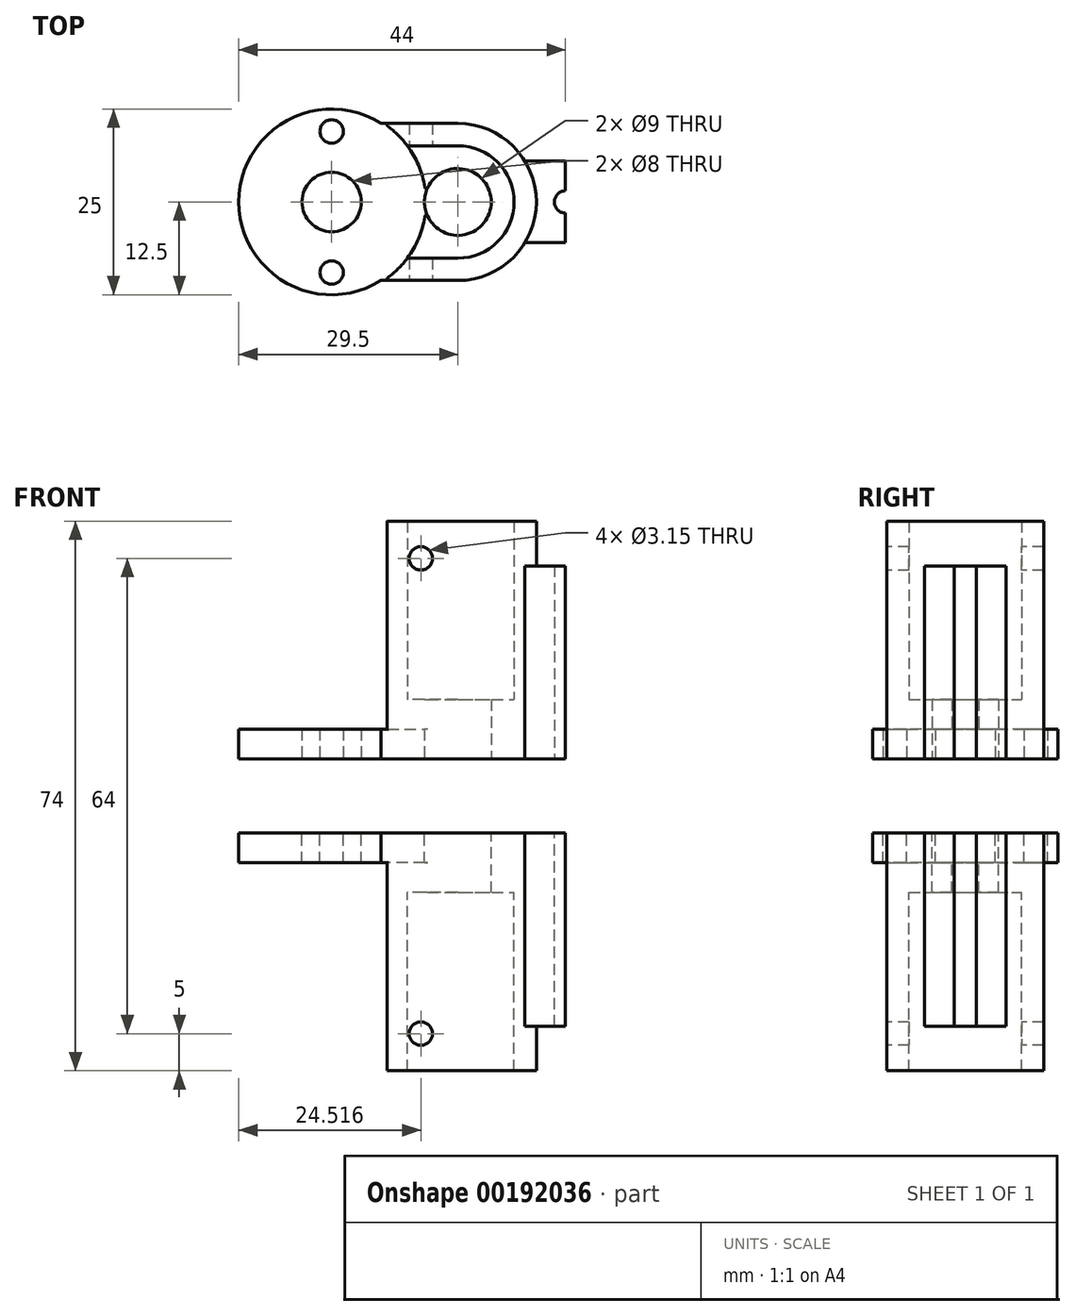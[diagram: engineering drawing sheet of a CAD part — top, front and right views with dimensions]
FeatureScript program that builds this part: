
annotation { "Feature Type Name" : "Feature", "Feature Type Description" : "" }
export const myFeature = defineFeature(function(context is Context, id is Id, definition is map)
    precondition{}
    {
        {
            var Q0;
            Q0=qCreatedBy(makeId("Top.planeOp"),FACE);
            var sketch = newSketch(context, id + "F0", { "sketchPlane" : qUnion([Q0])});
            skCircle(sketch, "E0", {"center": v(0, 0) * mm, "radius": 4 * mm, "construction": true});
            skCircle(sketch, "E1", {"center": v(17, 0) * mm, "radius": 4.5 * mm, "construction": true});
            skCircle(sketch, "E2", {"center": v(17, 0) * mm, "radius": 7.58 * mm, "construction": true});
            skCircle(sketch, "E3", {"center": v(31.5, 0) * mm, "radius": 9 * mm, "construction": true});
            skArc(sketch, "E4", {"start": v(31.5, 7.5) * mm, "mid": v(39, 0) * mm, "end": v(31.5, -7.5) * mm, "construction": true});
            skLineSegment(sketch, "E5", {"start": v(31.5, 7.5) * mm, "end": v(-52.72, 7.5) * mm, "construction": true});
            skLineSegment(sketch, "E6", {"start": v(31.5, -7.5) * mm, "end": v(-52.72, -7.5) * mm, "construction": true});
            skCircle(sketch, "E7", {"center": v(31.5, 0) * mm, "radius": 1.5 * mm, "construction": true});
            skArc(sketch, "E8", {"start": v(31.5, 5.5) * mm, "mid": v(37, 0) * mm, "end": v(31.5, -5.5) * mm, "construction": true});
            skLineSegment(sketch, "E9", {"start": v(31.5, 5.5) * mm, "end": v(-52.72, 5.5) * mm, "construction": true});
            skLineSegment(sketch, "E10", {"start": v(31.5, -5.5) * mm, "end": v(-52.72, -5.5) * mm, "construction": true});
            skCircle(sketch, "E11", {"center": v(0, 0) * mm, "radius": 12.5 * mm, "construction": true});
            skLineSegment(sketch, "E12", {"start": v(-52.72, 7.5) * mm, "end": v(-52.72, 5.5) * mm, "construction": true});
            skLineSegment(sketch, "E13", {"start": v(-52.72, -5.5) * mm, "end": v(-52.72, -7.5) * mm, "construction": true});
            skLineSegment(sketch, "E14", {"start": v(22.5, 0) * mm, "end": v(21.5, 0) * mm, "construction": true});
            skCircle(sketch, "E15", {"center": v(0, 9.5) * mm, "radius": 1.57 * mm, "construction": true});
            skCircle(sketch, "E16.MirrorC", {"center": v(0, -9.5) * mm, "radius": 1.57 * mm, "construction": true});
            skSolve(sketch);
        }
        {
            var Q0;
            Q0=qCreatedBy(makeId("Front.planeOp"),FACE);
            var sketch = newSketch(context, id + "F1", { "sketchPlane" : qUnion([Q0])});
            skLineSegment(sketch, "E17.bottom", {"start": v(-49.85, 26.5) * mm, "end": v(65.27, 26.5) * mm});
            skLineSegment(sketch, "E17.top", {"start": v(-49.85, 18.5) * mm, "end": v(65.27, 18.5) * mm});
            skLineSegment(sketch, "E17.left", {"start": v(-49.85, 26.5) * mm, "end": v(-49.85, 18.5) * mm});
            skLineSegment(sketch, "E17.right", {"start": v(65.27, 26.5) * mm, "end": v(65.27, 18.5) * mm});
            skLineSegment(sketch, "E18.MirrorCS", {"start": v(-49.85, -26.5) * mm, "end": v(-49.85, -18.5) * mm});
            skLineSegment(sketch, "E19.MirrorCS", {"start": v(-49.85, -26.5) * mm, "end": v(65.27, -26.5) * mm});
            skLineSegment(sketch, "E20.MirrorCS", {"start": v(-49.85, -18.5) * mm, "end": v(65.27, -18.5) * mm});
            skLineSegment(sketch, "E21.MirrorCS", {"start": v(65.27, -26.5) * mm, "end": v(65.27, -18.5) * mm});
            skPoint(sketch, "E22", {"position": v(-49.85, 22.5) * mm});
            skPoint(sketch, "E23", {"position": v(-49.85, -22.5) * mm});
            skSolve(sketch);
        }
        {
            var Q0;
            Q0=qCreatedBy(makeId("Top.planeOp"),FACE);
            var sketch = newSketch(context, id + "F2", { "sketchPlane" : qUnion([Q0])});
            skCircle(sketch, "E24.0", {"center": v(0, 0) * mm, "radius": 12.5 * mm, "construction": true});
            skCircle(sketch, "E25.0", {"center": v(17, 0) * mm, "radius": 7.58 * mm, "construction": true});
            skCircle(sketch, "E26.0", {"center": v(31.5, 0) * mm, "radius": 9 * mm, "construction": true});
            skCircle(sketch, "E27.0", {"center": v(17, 0) * mm, "radius": 10.58 * mm, "construction": true});
            skLineSegment(sketch, "E28", {"start": v(17, 10.58) * mm, "end": v(6.66, 10.57) * mm});
            skLineSegment(sketch, "E29", {"start": v(17, -10.58) * mm, "end": v(6.66, -10.58) * mm});
            skArc(sketch, "E30", {"start": v(6.66, 10.57) * mm, "mid": v(-12.5, 0) * mm, "end": v(6.66, -10.58) * mm});
            skArc(sketch, "E31.0", {"start": v(31.5, 5.5) * mm, "mid": v(37, 0) * mm, "end": v(31.5, -5.5) * mm, "construction": true});
            skLineSegment(sketch, "E32", {"start": v(31.5, 5.5) * mm, "end": v(26.03, 5.5) * mm});
            skLineSegment(sketch, "E33", {"start": v(31.5, -5.5) * mm, "end": v(26.03, -5.5) * mm});
            skArc(sketch, "E34", {"start": v(17, 10.58) * mm, "mid": v(22.18, 9.22) * mm, "end": v(26.03, 5.5) * mm});
            skArc(sketch, "E35", {"start": v(17, -10.58) * mm, "mid": v(22.18, -9.22) * mm, "end": v(26.03, -5.5) * mm});
            skCircle(sketch, "E36.0", {"center": v(0, 0) * mm, "radius": 4 * mm});
            skCircle(sketch, "E37.0", {"center": v(31.5, 0) * mm, "radius": 1.5 * mm});
            skCircle(sketch, "E38.0", {"center": v(17, 0) * mm, "radius": 4.5 * mm});
            skLineSegment(sketch, "E39", {"start": v(31.5, 5.5) * mm, "end": v(31.5, 1.5) * mm});
            skLineSegment(sketch, "E40", {"start": v(31.5, -5.5) * mm, "end": v(31.5, -1.5) * mm});
            skCircle(sketch, "E41.0", {"center": v(0, 9.5) * mm, "radius": 1.57 * mm});
            skCircle(sketch, "E42.0", {"center": v(0, -9.5) * mm, "radius": 1.57 * mm});
            skSolve(sketch);
        }
        {
            var Q0;
            Q0=qCreatedBy(makeId("Top.planeOp"),FACE);
            var sketch = newSketch(context, id + "F3", { "sketchPlane" : qUnion([Q0])});
            skLineSegment(sketch, "E43.0", {"start": v(31.5, 5.5) * mm, "end": v(-52.72, 5.5) * mm});
            skLineSegment(sketch, "E44.0", {"start": v(31.5, 7.5) * mm, "end": v(-52.72, 7.5) * mm});
            skLineSegment(sketch, "E45.0", {"start": v(-52.72, -5.5) * mm, "end": v(-52.72, -7.5) * mm});
            skLineSegment(sketch, "E46.0", {"start": v(31.5, -5.5) * mm, "end": v(-52.72, -5.5) * mm});
            skLineSegment(sketch, "E47.0", {"start": v(31.5, -7.5) * mm, "end": v(-52.72, -7.5) * mm});
            skArc(sketch, "E48.0", {"start": v(31.5, 5.5) * mm, "mid": v(37, 0) * mm, "end": v(31.5, -5.5) * mm});
            skArc(sketch, "E49.0", {"start": v(31.5, 7.5) * mm, "mid": v(39, 0) * mm, "end": v(31.5, -7.5) * mm});
            skLineSegment(sketch, "E50.0", {"start": v(-52.72, 7.5) * mm, "end": v(-52.72, 5.5) * mm});
            skSolve(sketch);
        }
        {
            var Q0;
            Q0=makeQuery(id+"F2.imprint","IMPRINT",FACE,{"disambiguationData":[TD([[makeQuery(id+"F2.imprint","IMPRINT",EDGE,{"derivedFrom":sQuery(id+"F2.wireOp",EDGE,"E28")}),1.0]])]});
            extrude(context, id + "F4", {"entities" : qUnion([Q0]), "depth" : 4 * mm});
        }
        {
            var Q0;
            Q0=makeQuery(id+"F4.opExtrude","CAP_FACE",FACE,{"disambiguationData":[OSD([sQuery(id+"F2.wireOp",EDGE,"E28"),sQuery(id+"F2.wireOp",EDGE,"E29"),sQuery(id+"F2.wireOp",EDGE,"E30"),sQuery(id+"F2.wireOp",EDGE,"E31.0"),sQuery(id+"F2.wireOp",EDGE,"E32"),sQuery(id+"F2.wireOp",EDGE,"E33"),sQuery(id+"F2.wireOp",EDGE,"E34"),sQuery(id+"F2.wireOp",EDGE,"E35"),sQuery(id+"F2.wireOp",EDGE,"E36.0"),sQuery(id+"F2.wireOp",EDGE,"E37.0"),sQuery(id+"F2.wireOp",EDGE,"E38.0")])],"isStart":false});
            var sketch = newSketch(context, id + "F5", { "sketchPlane" : qUnion([Q0])});
            skCircle(sketch, "E51.0", {"center": v(17, 0) * mm, "radius": 4.5 * mm});
            skArc(sketch, "E52", {"start": v(17, 10.58) * mm, "mid": v(27.58, 0) * mm, "end": v(17, -10.58) * mm});
            skArc(sketch, "E53", {"start": v(6.66, 10.57) * mm, "mid": v(12.5, 0) * mm, "end": v(6.66, -10.58) * mm, "construction": true});
            skArc(sketch, "E54.0", {"start": v(7.03, 10.57) * mm, "mid": v(12.7, 0) * mm, "end": v(7.03, -10.58) * mm});
            skLineSegment(sketch, "E55", {"start": v(17, 10.57) * mm, "end": v(7.03, 10.57) * mm});
            skLineSegment(sketch, "E56", {"start": v(17, -10.58) * mm, "end": v(7.03, -10.58) * mm});
            skSolve(sketch);
        }
        {
            var Q0;
            {var subQ7=sQuery(id+"F5.wireOp",EDGE,"E55");Q0=makeQuery(id+"F5.imprint","IMPRINT",FACE,{"disambiguationData":[TD([[makeQuery(id+"F5.imprint","IMPRINT",EDGE,{"derivedFrom":subQ7}),1.0]])]});}
            extrude(context, id + "F6", {"entities" : qUnion([Q0]), "operationType" : NewBodyOperationType.ADD, "depth" : 4 * mm});
        }
        {
            var Q0;
            Q0=makeQuery(id+"F6.opExtrude","CAP_FACE",FACE,{"disambiguationData":[OSD([sQuery(id+"F5.wireOp",EDGE,"E51.0"),sQuery(id+"F5.wireOp",EDGE,"E52"),sQuery(id+"F5.wireOp",EDGE,"BbAhyjgk-xgWP-F3I1-mA0A-6WR5w57MHJqB"),sQuery(id+"F5.wireOp",EDGE,"622a587f-51d2-48ef-ab83-598356b288d1.0"),sQuery(id+"F5.wireOp",EDGE,"a473993c-0456-45ff-bfd1-ddf6d82de39f.0")])],"isStart":false});
            var sketch = newSketch(context, id + "F7", { "sketchPlane" : qUnion([Q0])});
            skCircle(sketch, "E57.0", {"center": v(17, 0) * mm, "radius": 7.58 * mm, "construction": true});
            skArc(sketch, "E58", {"start": v(17, 7.58) * mm, "mid": v(24.57, 0) * mm, "end": v(17, -7.58) * mm});
            skArc(sketch, "E59", {"start": v(17, 10.58) * mm, "mid": v(27.58, 0) * mm, "end": v(17, -10.58) * mm});
            skLineSegment(sketch, "E60", {"start": v(17, -7.58) * mm, "end": v(10.2, -7.58) * mm});
            skLineSegment(sketch, "E61", {"start": v(17, -10.58) * mm, "end": v(7.03, -10.58) * mm});
            skArc(sketch, "E62.0", {"start": v(7.03, 10.57) * mm, "mid": v(8.74, 9.21) * mm, "end": v(10.2, 7.58) * mm});
            skLineSegment(sketch, "E63.MirrorCS", {"start": v(17, 7.58) * mm, "end": v(10.2, 7.58) * mm});
            skLineSegment(sketch, "E64.MirrorCS", {"start": v(17, 10.58) * mm, "end": v(7.03, 10.58) * mm});
            skArc(sketch, "E65.trimOffspring", {"start": v(10.2, -7.58) * mm, "mid": v(8.74, -9.21) * mm, "end": v(7.03, -10.58) * mm});
            skSolve(sketch);
        }
        {
            var Q0;
            Q0 = qSketchRegion(id + "F7", true);
            extrude(context, id + "F8", {"entities" : qUnion([Q0]), "operationType" : NewBodyOperationType.ADD, "depth" : 24 * mm});
        }
        {
            var Q0;
            Q0=makeQuery(id+"F8.boolean.opBoolean","MERGE",FACE,{"derivedFrom":[makeQuery(id+"F6.boolean.opBoolean","MERGE",FACE,{"derivedFrom":[makeQuery(id+"F4.opExtrude","SWEPT_FACE",FACE,{"disambiguationData":[OSD([sQuery(id+"F2.wireOp",EDGE,"E29")])]}),makeQuery(id+"F6.opExtrude","SWEPT_FACE",FACE,{"disambiguationData":[OSD([sQuery(id+"F5.wireOp",EDGE,"E56")])]})]}),makeQuery(id+"F8.opExtrude","SWEPT_FACE",FACE,{"disambiguationData":[OSD([sQuery(id+"F7.wireOp",EDGE,"E61")])]})]});
            var sketch = newSketch(context, id + "F9", { "sketchPlane" : qUnion([Q0])});
            skCircle(sketch, "E66", {"center": v(12.02, 27) * mm, "radius": 1.57 * mm});
            skLineSegment(sketch, "E67", {"start": v(12.02, 32) * mm, "end": v(12.02, 27) * mm, "construction": true});
            skSolve(sketch);
        }
        {
            var Q0;
            Q0 = qSketchRegion(id + "F9", true);
            var Q1;
            Q1=makeQuery(id+"F8.opExtrude","SWEPT_FACE",FACE,{"disambiguationData":[OSD([sQuery(id+"F7.wireOp",EDGE,"E60")])]});
            extrude(context, id + "F10", {"entities" : qUnion([Q0]), "operationType" : NewBodyOperationType.REMOVE, "endBound" : BoundingType.THROUGH_ALL, "oppositeDirection" : true, "endBoundEntityFace" : qUnion([Q1]), "depth" : 25 * mm});
        }
        {
            var Q0;
            {var subQ0=makeQuery(id+"F4.opExtrude","CAP_EDGE",EDGE,{"disambiguationData":[OSD([sQuery(id+"F2.wireOp",EDGE,"E32")])],"isStart":false});Q0=makeQuery(id+"F5.imprint","IMPRINT",FACE,{"disambiguationData":[TD([[makeQuery(id+"F5.imprint","IMPRINT",EDGE,{"derivedFrom":subQ0}),1.0]])]});}
            extrude(context, id + "F11", {"entities" : qUnion([Q0]), "operationType" : NewBodyOperationType.ADD, "depth" : (25 - 3) * mm});
        }
        {
            var Q0;
            Q0=makeQuery(id+"F8.boolean.opBoolean","MERGE",EDGE,{"derivedFrom":[makeQuery(id+"F6.opExtrude","SWEPT_EDGE",EDGE,{"disambiguationData":[OSD([sQuery(id+"F2.wireOp",EDGE,"E29"),sQuery(id+"F5.wireOp",EDGE,"E54.0"),sQuery(id+"F5.wireOp",EDGE,"E56")])]}),makeQuery(id+"F8.opExtrude","SWEPT_EDGE",EDGE,{"disambiguationData":[OSD([sQuery(id+"F7.wireOp",EDGE,"E61"),sQuery(id+"F7.wireOp",EDGE,"E62.0")])]})]});
            var Q1;
            Q1=makeQuery(id+"F6.opExtrude","SWEPT_EDGE",EDGE,{"disambiguationData":[OSD([sQuery(id+"F2.wireOp",EDGE,"E28"),sQuery(id+"F5.wireOp",EDGE,"E54.0"),sQuery(id+"F5.wireOp",EDGE,"E55")])]});
            var Q2;
            {var subQ0=sQuery(id+"F5.wireOp",EDGE,"E54.0");var subQ1=sQuery(id+"F5.wireOp",EDGE,"E51.0");Q2=makeQuery(id+"F6.opExtrude","SWEPT_EDGE",EDGE,{"disambiguationData":[OSD([subQ1,subQ0]),TDD([makeQuery(id+"F5.imprint","INTERSECT",VERTEX,{"disambiguationData":[OD(0.0)],"derivedFrom":[subQ1,subQ0]})])]});}
            var Q3;
            {var subQ0=sQuery(id+"F5.wireOp",EDGE,"E54.0");var subQ1=sQuery(id+"F5.wireOp",EDGE,"E51.0");Q3=makeQuery(id+"F6.opExtrude","SWEPT_EDGE",EDGE,{"disambiguationData":[OSD([subQ1,subQ0]),TDD([makeQuery(id+"F5.imprint","INTERSECT",VERTEX,{"disambiguationData":[OD(1.0)],"derivedFrom":[subQ1,subQ0]})])]});}
            fillet(context, id + "F12", {"entities" : qUnion([Q0, Q1, Q2, Q3]), "radius" : 0.2 * mm, "allowEdgeOverflow" : false});
        }
        {
            var Q0;
            Q0=makeQuery(id+"F4.opExtrude","SWEPT_BODY",BODY,{"disambiguationData":[OSD([sQuery(id+"F2.wireOp",EDGE,"E28"),sQuery(id+"F2.wireOp",EDGE,"E29"),sQuery(id+"F2.wireOp",EDGE,"E30"),sQuery(id+"F2.wireOp",EDGE,"E31.0"),sQuery(id+"F2.wireOp",EDGE,"E32"),sQuery(id+"F2.wireOp",EDGE,"E33"),sQuery(id+"F2.wireOp",EDGE,"E34"),sQuery(id+"F2.wireOp",EDGE,"E35"),sQuery(id+"F2.wireOp",EDGE,"E36.0"),sQuery(id+"F2.wireOp",EDGE,"E37.0"),sQuery(id+"F2.wireOp",EDGE,"E38.0")])]});
            transform(context, id + "F13", {"entities" : qUnion([Q0]), "transformType" : TransformType.TRANSLATION_3D, "dx" : 0 * mm, "dy" : 0 * mm, "dz" : 5 * mm, "makeCopy" : false});
        }
        {
            var Q0;
            Q0=makeQuery(id+"F4.opExtrude","SWEPT_BODY",BODY,{"disambiguationData":[OSD([sQuery(id+"F2.wireOp",EDGE,"E28"),sQuery(id+"F2.wireOp",EDGE,"E29"),sQuery(id+"F2.wireOp",EDGE,"E30"),sQuery(id+"F2.wireOp",EDGE,"E31.0"),sQuery(id+"F2.wireOp",EDGE,"E32"),sQuery(id+"F2.wireOp",EDGE,"E33"),sQuery(id+"F2.wireOp",EDGE,"E34"),sQuery(id+"F2.wireOp",EDGE,"E35"),sQuery(id+"F2.wireOp",EDGE,"E36.0"),sQuery(id+"F2.wireOp",EDGE,"E37.0"),sQuery(id+"F2.wireOp",EDGE,"E38.0")])]});
            var Q1;
            Q1=qCreatedBy(makeId("Top.planeOp"),FACE);
            mirror(context, id + "F14", {"entities" : qUnion([Q0]), "mirrorPlane" : qUnion([Q1])});
        }
    });
